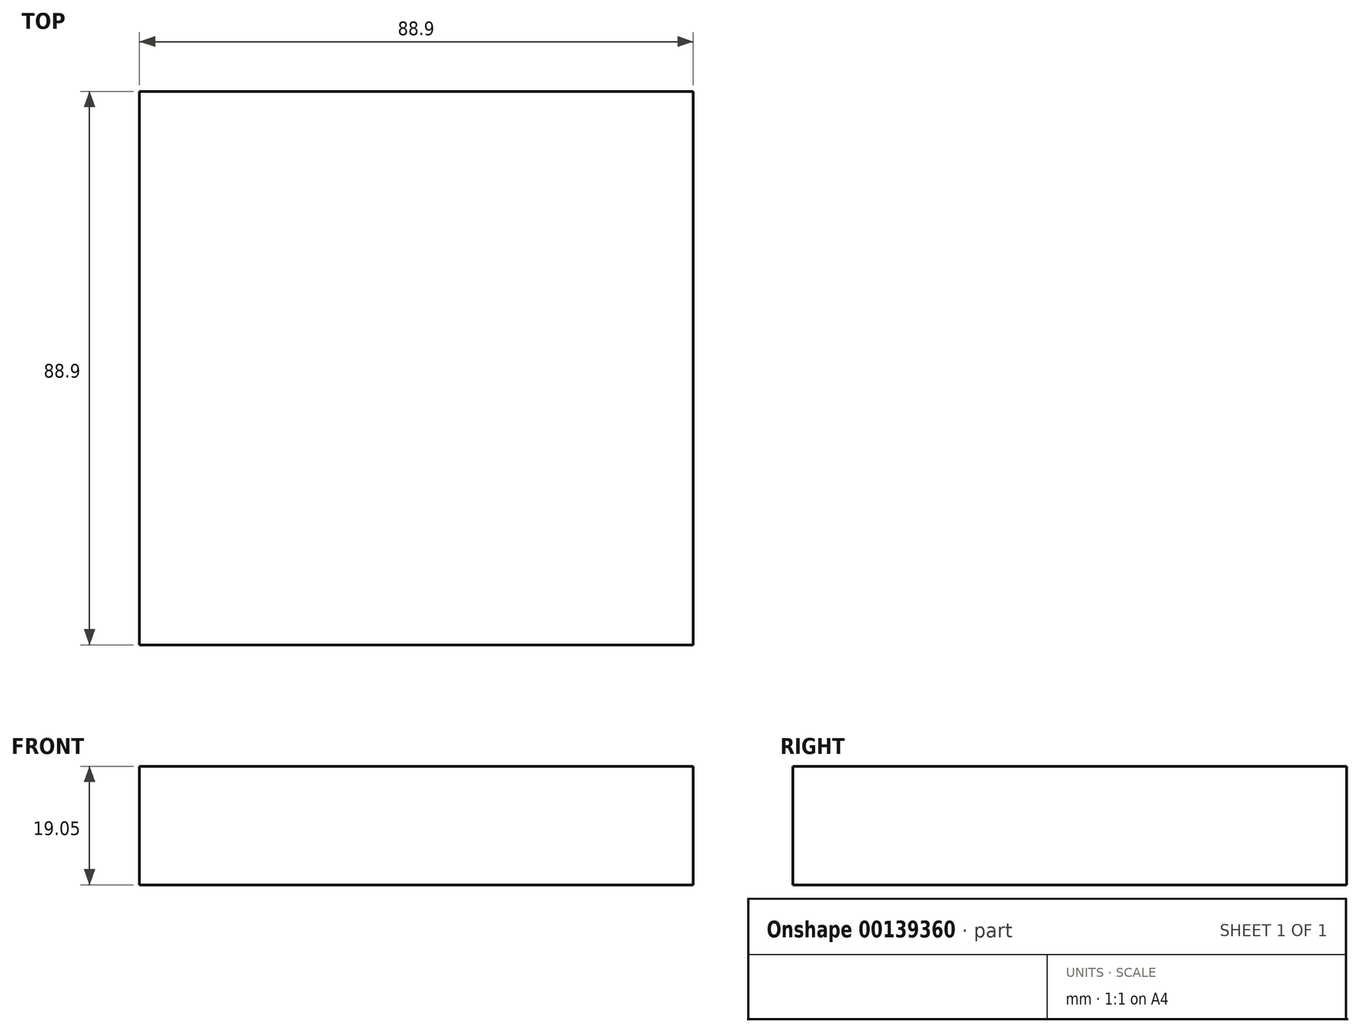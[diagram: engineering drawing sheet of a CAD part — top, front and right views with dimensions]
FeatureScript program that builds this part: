
annotation { "Feature Type Name" : "Feature", "Feature Type Description" : "" }
export const myFeature = defineFeature(function(context is Context, id is Id, definition is map)
    precondition{}
    {
        {
            var Q0;
            Q0=qCreatedBy(makeId("Top.planeOp"),FACE);
            var sketch = newSketch(context, id + "F1", { "sketchPlane" : qUnion([Q0])});
            skLineSegment(sketch, "E0.bottom", {"start": v(44.45, -44.45) * mm, "end": v(-44.45, -44.45) * mm});
            skLineSegment(sketch, "E0.top", {"start": v(44.45, 44.45) * mm, "end": v(-44.45, 44.45) * mm});
            skLineSegment(sketch, "E0.left", {"start": v(44.45, -44.45) * mm, "end": v(44.45, 44.45) * mm});
            skLineSegment(sketch, "E0.right", {"start": v(-44.45, -44.45) * mm, "end": v(-44.45, 44.45) * mm});
            skPoint(sketch, "E0.middle", {"position": v(0, 0) * mm});
            skSolve(sketch);
        }
        {
            var Q0;
            Q0=makeQuery(id+"F1.imprint","IMPRINT",FACE,{"disambiguationData":[TD([[makeQuery(id+"F1.imprint","IMPRINT",EDGE,{"derivedFrom":sQuery(id+"F1.wireOp",EDGE,"E0.bottom")}),-1.0]])]});
            extrude(context, id + "F0", {"entities" : qUnion([Q0]), "depth" : 19.05 * mm});
        }
    });
